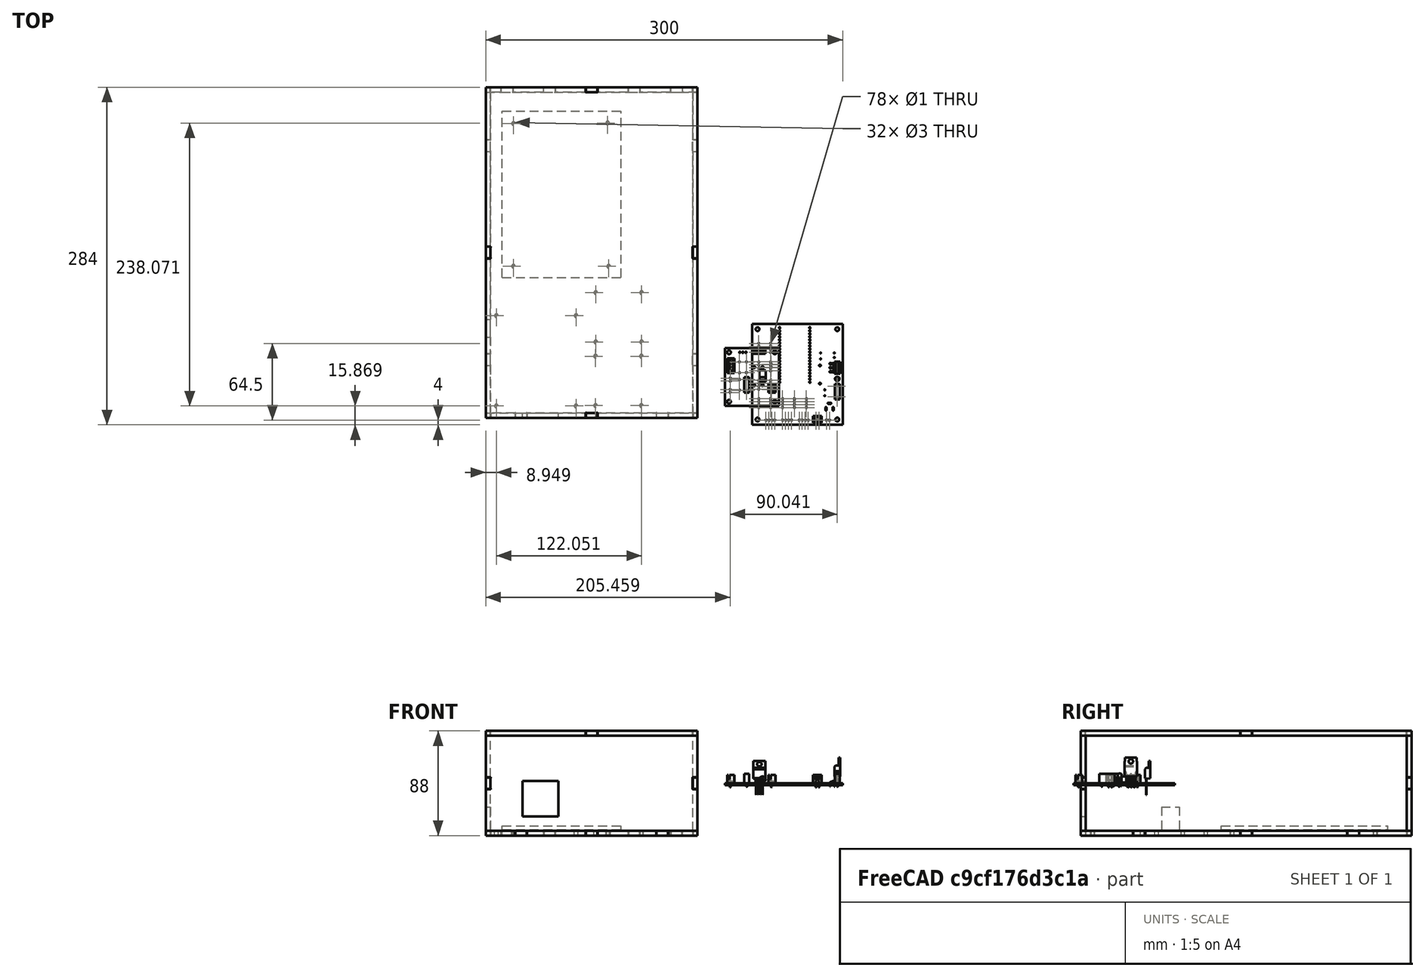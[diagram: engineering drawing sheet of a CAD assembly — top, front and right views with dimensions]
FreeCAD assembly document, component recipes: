
FREECAD ASSEMBLY — COMPONENT RECIPES ("enclosure")

This assembly document has 3 components, labeled P0..P2 below (a component is one placed body or linked part). 0 of them carry a construction recipe — the FreeCAD feature program that regenerates the part from scratch, quoted from this document or its linked companion documents; the rest are supplied as boundary geometry only. No exploded tour is included for this assembly.
COMPONENT P0 — geometry summary ("beehive001"; no construction recipe available for this part):
  bounding box: 85.0 x 76.0 x 24.9 mm
  tessellated surface: 37,130 triangles
  volume: 11421 mm^3 (7% of its bounding box)
COMPONENT P1 — geometry summary ("solenoid_driver"; no construction recipe available for this part):
  bounding box: 48.5 x 45.5 x 28.5 mm
  tessellated surface: 29,840 triangles
  volume: 7398 mm^3 (12% of its bounding box)
COMPONENT P2 — geometry summary ("solenoid_driver001"; no construction recipe available for this part):
  bounding box: 48.5 x 45.5 x 28.5 mm
  tessellated surface: 29,840 triangles
  volume: 7398 mm^3 (12% of its bounding box)
PROVENANCE & LICENSES
A FreeCAD (.FCStd) document from a public repository crawl; recipes are the document's own serialized feature recipes (and, for linked parts, companion documents' recipes).
License: gpl-3.0.
